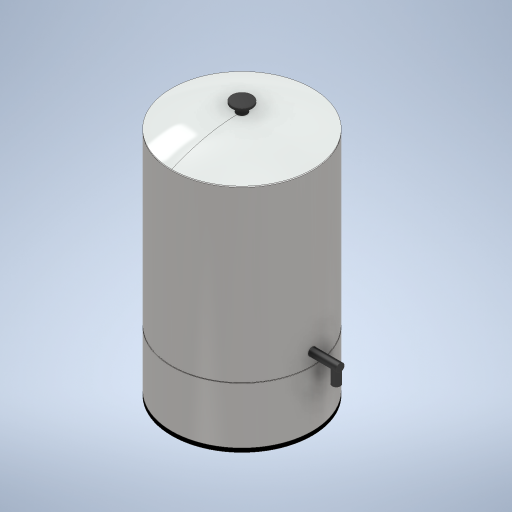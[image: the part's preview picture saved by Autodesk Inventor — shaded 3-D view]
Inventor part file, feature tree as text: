
AUTODESK INVENTOR PART (.ipt)
format: ipt  version: 2024 (Build 280153000, 153)  size: 375,296 bytes
history: native  units: mm
features: sketch x10, extrude x9, plane x3, fillet x2, revolve x1, chamfer x1, projected_geometry x1
ambient origin geometry x8: Origin, YZ Plane, XZ Plane, XY Plane, X Axis, Y Axis, Z Axis, Center Point
bodies: Solid1 (feature_tree)
feature tree (27):
  extrude  "Extrusion1"  Depth=2.0mm TaperAngle=0.0deg
  extrude  "Extrusion2"  Depth=1.0mm TaperAngle=0.0deg
  fillet  "Fillet2"  Radius=1.0mm
  extrude  "Extrusion5"  Depth=140.0mm TaperAngle=0.0deg
  fillet  "Fillet3"  Radius=1.0mm
  extrude  "Extrusion6"  Depth=10.0mm
  revolve  "Revolution1"  Angle=360.0deg
  plane  "Work Plane1"
  extrude  "Extrusion8"  Depth=25.0mm
  extrude  "Extrusion9"  Depth=15.0mm
  chamfer  "Chamfer1"  Distance=15.0mm
  plane  "Work Plane2"
  extrude  "Extrusion10"  Depth=10.0mm
  plane  "Work Plane4"
  extrude  "Extrusion11"  Depth=70.0mm TaperAngle=0.0deg
  extrude  "Extrusion12"  Depth=10.0mm TaperAngle=0.0deg
  sketch  "Sketch1"  dims[d0=350.0mm d1=2.0mm d2=0.0mm]
  sketch  "Sketch2"  dims[d3=349.0mm d4=420.0mm d5=0.0mm d12=1.0mm]
  sketch  "Sketch5"  dims[d13=349.0mm d14=140.0mm d15=0.0mm d16=1.0mm]
  sketch  "Sketch6"  dims[d17=10.0mm d18=0.0mm d22=3.0mm]
  sketch  "Sketch9"  dims[d24=3.0mm d25=360.0deg]
  sketch  "Sketch10"  dims[d26=39.0mm d27=25.0mm]
  sketch  "Sketch11"  dims[d28=10.0mm d29=0.0mm d30=50.0mm d31=15.0mm d32=0.0mm]
  sketch  "Sketch12"  dims[d33=10.0mm d34=2.0mm d35=45.0deg d36=32.0mm]
  sketch  "Sketch13"  dims[d37=20.0mm d38=70.0mm d39=0.0mm]
  sketch  "Sketch14"  dims[d40=20.0mm d41=10.0mm d42=0.0mm d43=30.0mm d44=0.0mm]
  projected_geometry  "Projected Loop1"
